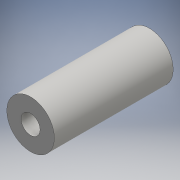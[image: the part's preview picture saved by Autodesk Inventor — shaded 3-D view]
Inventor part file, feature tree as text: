
AUTODESK INVENTOR PART (.ipt)
format: ipt  version: 2016 (Build 200138000, 138)  size: 108,544 bytes
history: native  units: mm
features: extrude x2, sketch x2
ambient origin geometry x8: Origin, YZ Plane, XZ Plane, XY Plane, X Axis, Y Axis, Z Axis, Center Point
bodies: 实体1 (feature_tree)
feature tree (4):
  extrude  "拉伸1"  Depth=25.0mm TaperAngle=0.0deg
  extrude  "拉伸3"  Depth=3.0mm TaperAngle=0.0deg
  sketch  "草图1"  dims[d0=10.0mm d2=25.0mm d3=0.0mm]
  sketch  "草图3"  dims[d7=4.0mm d8=3.0mm d9=0.0mm]
